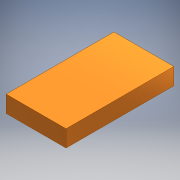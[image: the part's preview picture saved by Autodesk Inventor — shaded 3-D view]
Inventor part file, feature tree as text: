
AUTODESK INVENTOR PART (.ipt)
format: ipt  version: 2016 (Build 200138000, 138)  size: 87,040 bytes
history: native  units: mm
features: extrude x1, sketch x1
ambient origin geometry x8: Origin, YZ Plane, XZ Plane, XY Plane, X Axis, Y Axis, Z Axis, Center Point
bodies: Solid1 (feature_tree)
feature tree (2):
  extrude  "Extrusion1"  Depth=20.0mm
  sketch  "Sketch1"  dims[d0=36.0mm d1=20.0mm d2=5.6mm d3=0.0mm]
